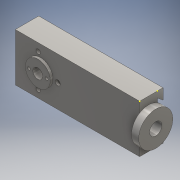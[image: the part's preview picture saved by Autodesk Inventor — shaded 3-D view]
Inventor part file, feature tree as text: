
AUTODESK INVENTOR PART (.ipt)
format: ipt  version: 2016 (Build 200138000, 138)  size: 230,912 bytes
history: native  units: mm
features: sketch x12, extrude x10
ambient origin geometry x8: Origin, YZ Plane, XZ Plane, XY Plane, X Axis, Y Axis, Z Axis, Center Point
bodies: Solid1 (feature_tree)
feature tree (22):
  extrude  "Extrusion1"  Depth=41.4mm
  extrude  "Extrusion2"  Depth=220.0mm
  extrude  "Extrusion3"  Depth=301.25mm TaperAngle=0.0deg
  sketch  "Sketch4"  dims[d12=15.1mm d13=15.1mm]
  extrude  "Extrusion4"  Depth=15.1mm
  sketch  "Sketch6"  dims[d17=28.6mm d18=30.2mm]
  extrude  "Extrusion5"  Depth=26.9mm TaperAngle=0.0deg
  extrude  "Extrusion6"  Depth=30.2mm
  extrude  "Extrusion7"  Depth=11.0mm
  extrude  "Extrusion8"  Depth=60.4mm
  extrude  "Extrusion9"  Depth=12.7mm
  extrude  "Extrusion10"  TaperAngle=90.0deg  [1 undecoded]
  sketch  "Sketch1"  dims[d0=85.0mm d1=41.4mm]
  sketch  "Sketch2"  dims[d2=220.0mm d3=0.0mm d4=19.0mm]
  sketch  "Sketch3"  dims[d8=19.0mm d9=301.25mm d10=0.0mm]
  sketch  "Sketch5"  dims[d14=141.9mm d15=26.9mm d16=0.0mm]
  sketch  "Sketch7"  dims[d19=4.6mm d21=11.0mm]
  sketch  "Sketch8"  dims[d22=91.9mm d23=0.0mm d24=60.4mm]
  sketch  "Sketch9"  dims[d25=12.7mm d26=0.0mm d27=10.6mm]
  sketch  "Sketch10"  dims[d28=83.6mm d29=90.0deg]
  sketch  "Sketch11"  dims[d30=4.9mm]
  sketch  "Sketch12"  dims[d31=6.0mm d32=0.0mm d33=22.0mm d34=22.3mm d35=22.7mm d36=22.15mm d37=0.0mm d38=4.6mm d39=0.0mm d40=17.5mm d41=310.85mm d42=0.0mm d43=4.4mm d44=5.0mm d45=4.4mm d46=2.5mm d47=3.5mm d48=0.0mm d49=40.7mm d50=9.4mm d51=4.0mm d52=40.7mm d53=9.4mm d54=4.0mm d55=70.6mm d56=39.5mm d57=4.5mm d58=4.5mm d59=7.0mm d60=0.0mm d61=8.726646mm d63=8.726646mm d64=10.0mm]
note: 1 required parameter value undecoded (feature->parameter linkage not recoverable at this tier; creation-order binding heuristic only, values carry confidence <= 0.55)
